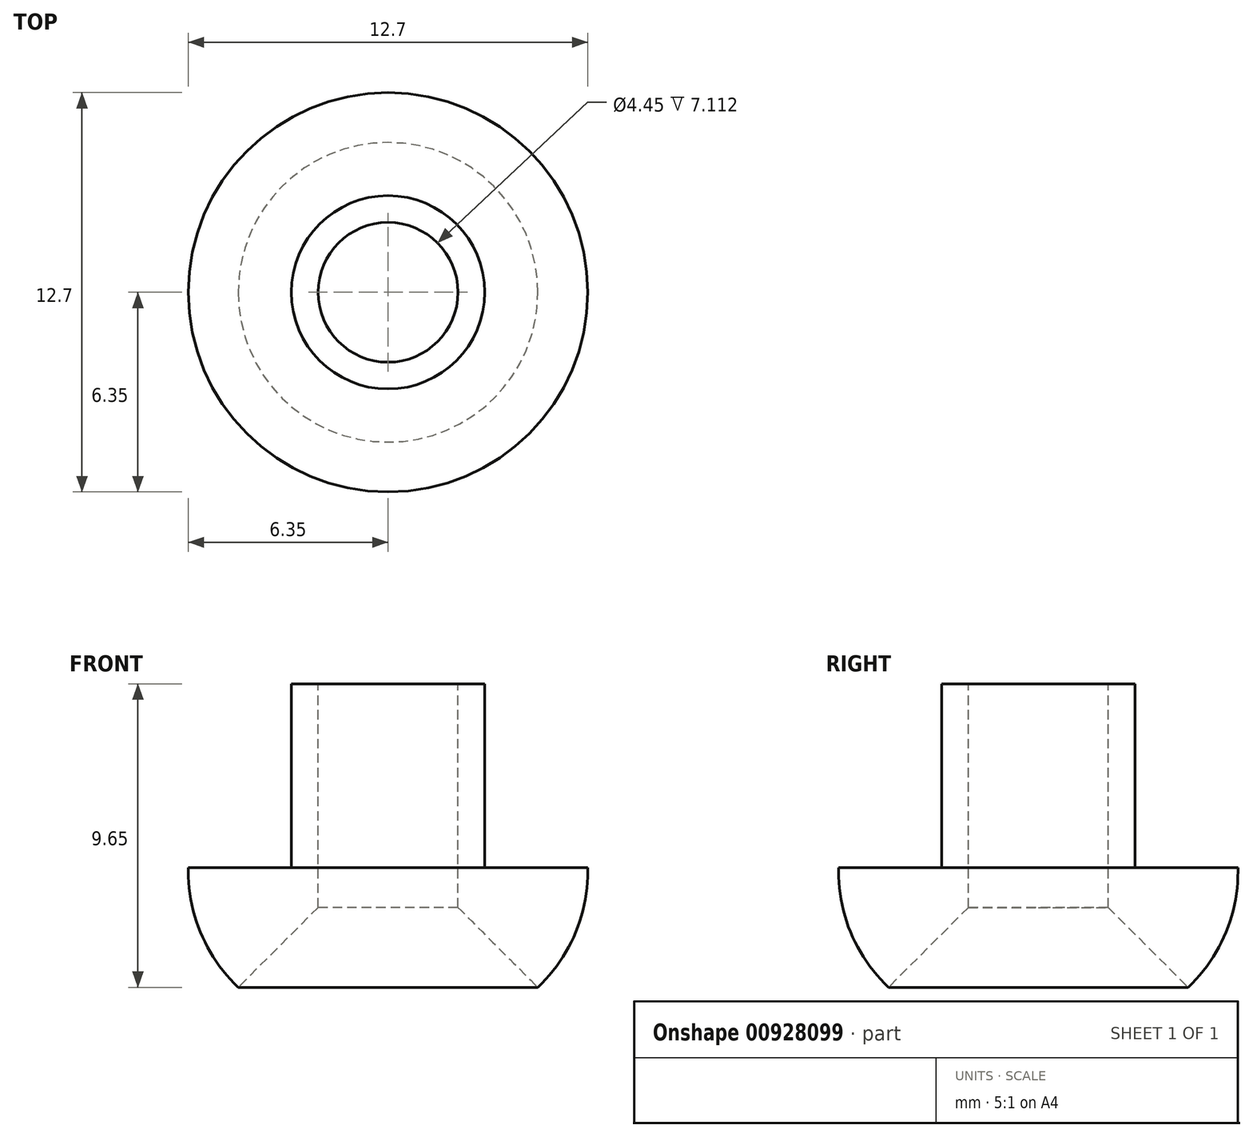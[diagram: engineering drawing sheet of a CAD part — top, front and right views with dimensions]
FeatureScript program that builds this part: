
annotation { "Feature Type Name" : "Feature", "Feature Type Description" : "" }
export const myFeature = defineFeature(function(context is Context, id is Id, definition is map)
    precondition{}
    {
        {
            var Q0;
            Q0=qCreatedBy(makeId("Top.planeOp"),FACE);
            var sketch = newSketch(context, id + "F0", { "sketchPlane" : qUnion([Q0])});
            skCircle(sketch, "E0", {"center": v(0, 0) * mm, "radius": 6.35 * mm});
            skSolve(sketch);
        }
        {
            var Q0;
            Q0 = qSketchRegion(id + "F0", true);
            extrude(context, id + "F1", {"entities" : qUnion([Q0]), "depth" : 3.8 * mm, "offsetDistance" : 25.4 * mm});
        }
        {
            var Q0;
            Q0=makeQuery(id+"F1.opExtrude","CAP_FACE",FACE,{"disambiguationData":[OSD([sQuery(id+"F0.wireOp",EDGE,"E0")])],"isStart":false});
            var sketch = newSketch(context, id + "F2", { "sketchPlane" : qUnion([Q0])});
            skCircle(sketch, "E1", {"center": v(0, 0) * mm, "radius": 3.07 * mm});
            skSolve(sketch);
        }
        {
            var Q0;
            Q0 = qSketchRegion(id + "F2", true);
            extrude(context, id + "F3", {"entities" : qUnion([Q0]), "operationType" : NewBodyOperationType.ADD, "depth" : 5.84 * mm, "offsetDistance" : 25.4 * mm});
        }
        {
            var Q0;
            Q0=makeQuery(id+"F3.opExtrude","CAP_FACE",FACE,{"disambiguationData":[OSD([sQuery(id+"F2.wireOp",EDGE,"E1")])],"isStart":false});
            var sketch = newSketch(context, id + "F4", { "sketchPlane" : qUnion([Q0])});
            skCircle(sketch, "E2", {"center": v(0, 0) * mm, "radius": 2.22 * mm});
            skSolve(sketch);
        }
        {
            var Q0;
            Q0 = qSketchRegion(id + "F4", true);
            extrude(context, id + "F5", {"entities" : qUnion([Q0]), "operationType" : NewBodyOperationType.REMOVE, "endBound" : BoundingType.THROUGH_ALL, "oppositeDirection" : true, "depth" : 25.4 * mm, "offsetDistance" : 25.4 * mm});
        }
        {
            var Q0;
            Q0=makeQuery(id+"F5.boolean.opBoolean","INTERSECT",EDGE,{"derivedFrom":[makeQuery(id+"F1.opExtrude","CAP_FACE",FACE,{"disambiguationData":[OSD([sQuery(id+"F0.wireOp",EDGE,"E0")])],"isStart":true}),makeQuery(id+"F5.opExtrude","SWEPT_FACE",FACE,{"disambiguationData":[OSD([sQuery(id+"F4.wireOp",EDGE,"E2")])]})]});
            chamfer(context, id + "F6", {"entities" : qUnion([Q0]), "chamferType" : ChamferType.OFFSET_ANGLE, "width" : 2.54 * mm, "oppositeDirection" : false, "angle" : 45 * degree, "tangentPropagation" : true});
        }
        {
            var Q0;
            Q0=makeQuery(id+"F1.opExtrude","CAP_EDGE",EDGE,{"disambiguationData":[OSD([sQuery(id+"F0.wireOp",EDGE,"E0")])],"isStart":true});
            fillet(context, id + "F7", {"entities" : qUnion([Q0]), "radius" : 5.08 * mm, "tangentPropagation" : true, "allowEdgeOverflow" : false});
        }
    });
